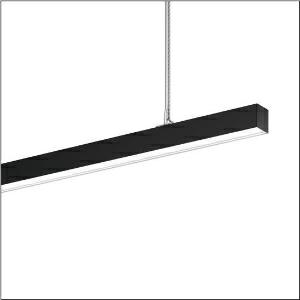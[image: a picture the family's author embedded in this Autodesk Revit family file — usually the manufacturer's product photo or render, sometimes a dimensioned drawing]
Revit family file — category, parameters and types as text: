
# Revit family: silica_r__21_51mx33dc3dbb_6d07
name_source: partatom
category: Lighting Fixtures
units: mm (PartAtom-declared; Revit-internal decimal feet)

## family parameters
Cut with Voids When Loaded = No
Host = Face
Light Source = No
Part Type = Normal
Room Calculation Point = No
Round Connector Dimension = Use Diameter
Shared = No

## types (1)
- --- (1 x LED, 14780 lm, 99.5 W, 3000K)
    Apparent Load = 100 VA
    CIE Flux Codes = 78 96 99 55 100
    Color Rendering = 80
    Color Temperature = 3000K
    Default Elevation = 1800 mm
    Description = Silica® 21, office luminaire, primary optical cover: prismatic diffuser, of PMMA, CAT 2 (L<= 3000cd/m²), light emission: direct/indirect distribution, primary light characteristic: symmetric, installation type: suspended mounting, LED, rated luminous flux: 14.780lm, luminous efficacy: 149lm/W, light colour: 830, colour temperature: 3000K, with terminal, 3+2-pole, max. 2.5mm², mains connection: 220..240V, AC, 50/60Hz, rated input power: 99.5W, luminaire housing, of aluminium, jet black (RAL 9005), length: 3.004mm, width: 53mm, height: 53mm, protection rating (complete): IP20, insulation class (complete): insulation class I (protective earthing), certification: CE, permissible operating ambient temperature: 0..+35°C, standard: EN 50419, packaging unit: 1 piece
    Height = 53 mm
    Lamp = 1 x LED
    Lamp Light Flux = 14780 lm
    Lamp Power = 99.5 W
    Lamp count = 1
    Length = 3004 mm
    Luminous efficacy = 149 lm/W
    Manufacturer = Siteco
    ModVariant = No
    Model = 51MX33DC3DBB
    Mounting Place = Ceiling
    Mounting Type = Pendant
    Number of Poles = 1
    OnlyDefault = Yes
    Power Factor = 1
    Product Name = Silica® 21
    Product group = office luminaire | ceiling pendant
    ProductGroupID = 902
    Protection Class = Protection class I
    Protection Degree = IP 20
    RLX_Detail_Level = 1
    RLX_Emergency_Light_Flux = 0 lm
    RLX_Emergency_Type = 0
    RLX_Emergency_Type_DB = No
    RlxData = <blob elided: 26205 chars, md5=a7bbbc34>
    Socket = socket
    Standby Power = 0 W
    System Light Flux = 14780 lm
    System Power = 100 W
    Type Comments = factory setting: luminous flux: 100 % | dim-lin: 254 | 345 mA
    Type Image = l_1297744.jpg
    URL = http://relux.com
    VarID = @adj_048987
    Voltage = 0 V
    Weight = 0.00 kg
    Width = 53 mm

## geometry (parser evidence)
native form markers: Blend x4, Sweep x13
no freeform markers — native parametric forms only
